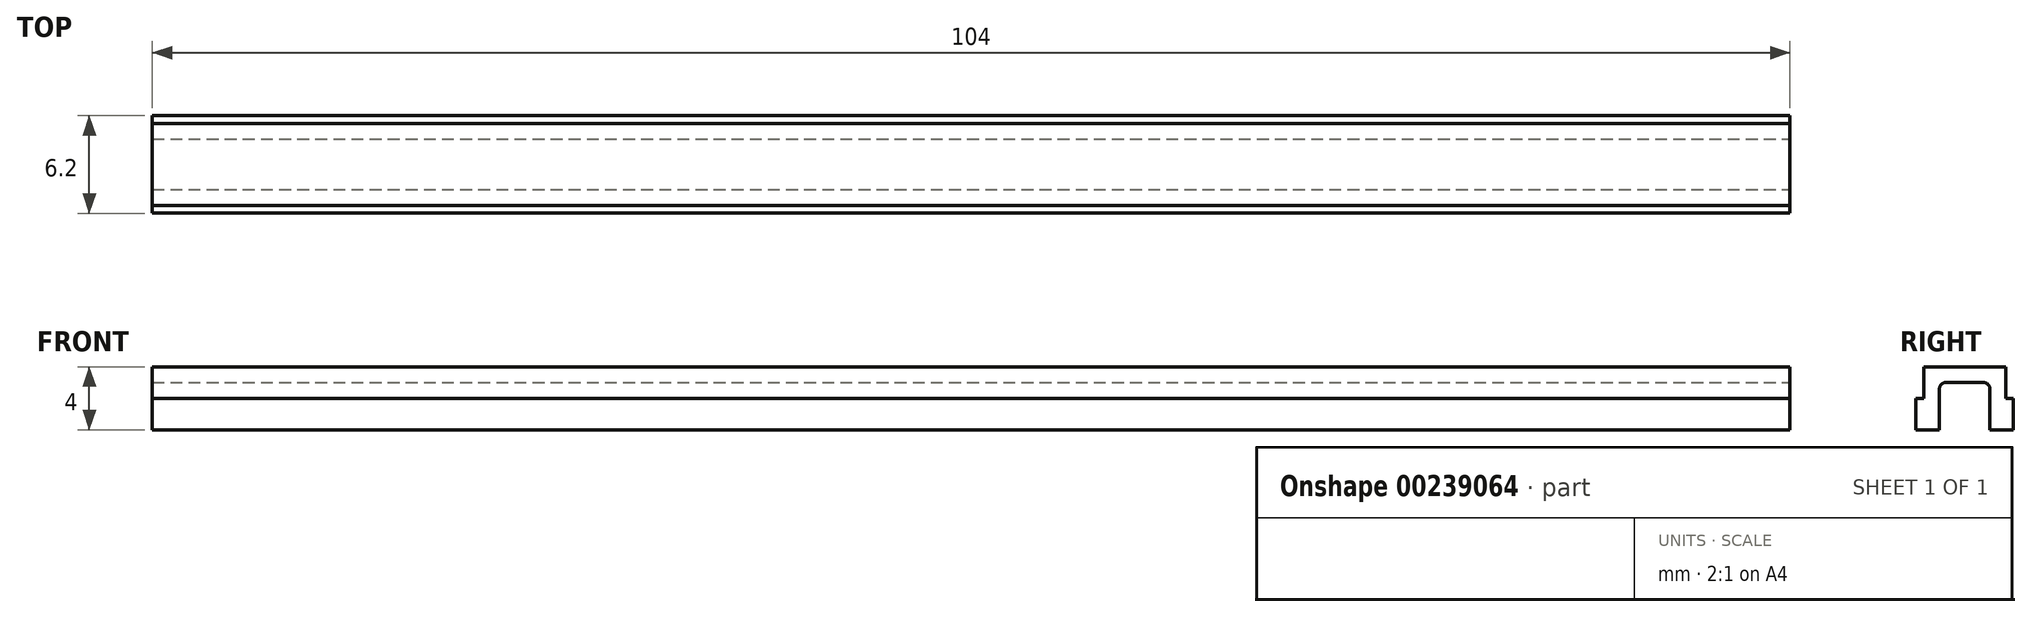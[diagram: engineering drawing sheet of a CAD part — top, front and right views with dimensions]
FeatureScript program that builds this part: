
annotation { "Feature Type Name" : "Feature", "Feature Type Description" : "" }
export const myFeature = defineFeature(function(context is Context, id is Id, definition is map)
    precondition{}
    {
        {
            var Q0;
            Q0=qCreatedBy(makeId("Top.planeOp"),FACE);
            var sketch = newSketch(context, id + "F0", { "sketchPlane" : qUnion([Q0])});
            skLineSegment(sketch, "E0.bottom", {"start": v(-44.35, -5.93) * mm, "end": v(59.65, -5.93) * mm});
            skLineSegment(sketch, "E0.top", {"start": v(-44.35, -11.13) * mm, "end": v(59.65, -11.13) * mm});
            skLineSegment(sketch, "E0.left", {"start": v(-44.35, -5.93) * mm, "end": v(-44.35, -11.13) * mm});
            skLineSegment(sketch, "E0.right", {"start": v(59.65, -5.93) * mm, "end": v(59.65, -11.13) * mm});
            skLineSegment(sketch, "E1.top", {"start": v(-44.35, -3.93) * mm, "end": v(59.65, -3.93) * mm});
            skLineSegment(sketch, "E1.left", {"start": v(-44.35, -5.93) * mm, "end": v(-44.35, -3.93) * mm});
            skLineSegment(sketch, "E1.right", {"start": v(59.65, -5.93) * mm, "end": v(59.65, -3.93) * mm});
            skLineSegment(sketch, "E2.top", {"start": v(-44.35, -13.13) * mm, "end": v(59.65, -13.13) * mm});
            skLineSegment(sketch, "E2.left", {"start": v(-44.35, -11.13) * mm, "end": v(-44.35, -13.13) * mm});
            skLineSegment(sketch, "E2.right", {"start": v(59.65, -11.13) * mm, "end": v(59.65, -13.13) * mm});
            skSolve(sketch);
        }
        {
            var Q0;
            Q0=makeQuery(id+"F0.imprint","IMPRINT",FACE,{"disambiguationData":[TD([[makeQuery(id+"F0.imprint","IMPRINT",EDGE,{"derivedFrom":sQuery(id+"F0.wireOp",EDGE,"E0.left")}),1.0]])]});
            extrude(context, id + "F1", {"entities" : qUnion([Q0]), "depth" : 3 * mm});
        }
        {
            var Q0;
            Q0 = qSketchRegion(id + "F0", true);
            extrude(context, id + "F2", {"entities" : qUnion([Q0]), "operationType" : NewBodyOperationType.ADD, "oppositeDirection" : true, "depth" : 1 * mm, "hasSecondDirection" : true, "secondDirectionOppositeDirection" : false, "secondDirectionDepth" : 1 * mm});
        }
        {
            var Q0;
            {var subQ0=sQuery(id+"F0.wireOp",EDGE,"E0.right");Q0=makeQuery(id+"F2.boolean.opBoolean","MERGE",FACE,{"derivedFrom":[makeQuery(id+"F1.opExtrude","SWEPT_FACE",FACE,{"disambiguationData":[OSD([subQ0])]}),makeQuery(id+"F2.opExtrude","SWEPT_FACE",FACE,{"disambiguationData":[OSD([subQ0,sQuery(id+"F0.wireOp",EDGE,"E1.right"),sQuery(id+"F0.wireOp",EDGE,"E2.right")])]})]});}
            var sketch = newSketch(context, id + "F3", { "sketchPlane" : qUnion([Q0])});
            skLineSegment(sketch, "E3.top", {"start": v(-3.93, -1) * mm, "end": v(-5.43, -1) * mm});
            skLineSegment(sketch, "E3.left", {"start": v(-3.93, 1) * mm, "end": v(-3.93, -1) * mm});
            skLineSegment(sketch, "E4.bottom", {"start": v(-10.13, -1) * mm, "end": v(-6.93, -1) * mm});
            skLineSegment(sketch, "E4.top", {"start": v(-9.73, 2) * mm, "end": v(-7.33, 2) * mm});
            skLineSegment(sketch, "E4.left", {"start": v(-10.13, -1) * mm, "end": v(-10.13, 1.6) * mm});
            skLineSegment(sketch, "E4.right", {"start": v(-6.93, -1) * mm, "end": v(-6.93, 1.6) * mm});
            skPoint(sketch, "E5.visualSharp", {"position": v(-10.13, 2) * mm});
            skArc(sketch, "E5.filletArc", {"start": v(-9.73, 2) * mm, "mid": v(-10, 1.88) * mm, "end": v(-10.13, 1.6) * mm});
            skPoint(sketch, "E6.visualSharp", {"position": v(-6.93, 2) * mm});
            skArc(sketch, "E6.filletArc", {"start": v(-6.93, 1.6) * mm, "mid": v(-7.04, 1.88) * mm, "end": v(-7.33, 2) * mm});
            skLineSegment(sketch, "E7.bottom", {"start": v(-13.13, 1) * mm, "end": v(-11.63, 1) * mm});
            skLineSegment(sketch, "E7.top", {"start": v(-13.13, -1) * mm, "end": v(-11.63, -1) * mm});
            skLineSegment(sketch, "E7.left", {"start": v(-13.13, 1) * mm, "end": v(-13.13, -1) * mm});
            skLineSegment(sketch, "E7.right", {"start": v(-11.63, 1) * mm, "end": v(-11.63, -1) * mm});
            skLineSegment(sketch, "E8.bottom", {"start": v(-3.93, 1) * mm, "end": v(-5.43, 1) * mm});
            skLineSegment(sketch, "E8.right", {"start": v(-5.43, 1) * mm, "end": v(-5.43, -1) * mm});
            skSolve(sketch);
        }
        {
            var Q0;
            Q0=makeQuery(id+"F3.imprint","IMPRINT",FACE,{"disambiguationData":[TD([[makeQuery(id+"F3.imprint","IMPRINT",EDGE,{"derivedFrom":sQuery(id+"F3.wireOp",EDGE,"E7.bottom")}),-1.0]])]});
            var Q1;
            Q1=makeQuery(id+"F3.imprint","IMPRINT",FACE,{"disambiguationData":[TD([[makeQuery(id+"F3.imprint","IMPRINT",EDGE,{"derivedFrom":sQuery(id+"F3.wireOp",EDGE,"E4.bottom")}),1.0]])]});
            var Q2;
            Q2=makeQuery(id+"F3.imprint","IMPRINT",FACE,{"disambiguationData":[TD([[makeQuery(id+"F3.imprint","IMPRINT",EDGE,{"derivedFrom":sQuery(id+"F3.wireOp",EDGE,"E8.bottom")}),-1.0]])]});
            extrude(context, id + "F4", {"entities" : qUnion([Q0, Q1, Q2]), "operationType" : NewBodyOperationType.REMOVE, "oppositeDirection" : true, "depth" : 104 * mm});
        }
    });
